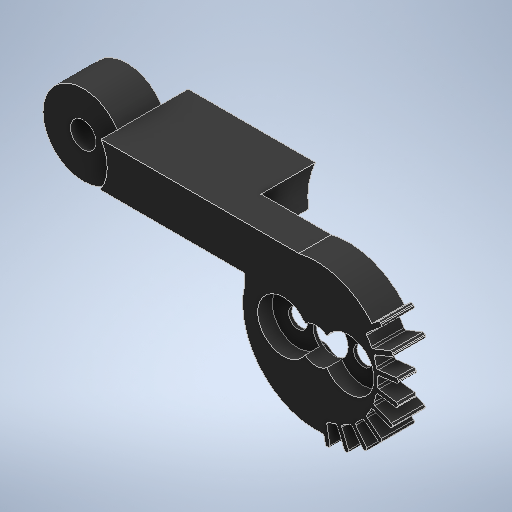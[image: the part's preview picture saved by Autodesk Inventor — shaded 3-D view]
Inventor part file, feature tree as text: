
AUTODESK INVENTOR PART (.ipt)
format: ipt  version: 2025.2 (Build 292293000, 293)  size: 515,072 bytes
history: native  units: mm
features: sketch x9, extrude x8, fillet x4, other x1, hole x1
ambient origin geometry x8: Origin, YZ Plane, XZ Plane, XY Plane, X Axis, Y Axis, Z Axis, Center Point
bodies: Body1 (feature_tree)
feature tree (23):
  other  "Sólido1"
  sketch  "Esboço1"  dims[d0=11.0mm d1=20.0mm]
  extrude  "Extrusão1"  Depth=11.0mm
  extrude  "Extrusão2"  Depth=6.8mm
  extrude  "Extrusão3"  Depth=21.0mm
  extrude  "Extrusão4"  Depth=6.0mm TaperAngle=0.0deg
  hole  "Furo2"  [1 undecoded]
  fillet  "Arredondamento1"  Radius=16.8mm
  fillet  "Arredondamento2"  Radius=8.726646mm
  fillet  "Arredondamento3"  Radius=1.3mm
  fillet  "Arredondamento4"  Radius=0.65mm
  extrude  "Extrusão5"  TaperAngle=90.0deg  [1 undecoded]
  extrude  "Extrusão6"  TaperAngle=90.0deg  [1 undecoded]
  extrude  "Extrusão7"  Depth=70.0mm TaperAngle=90.0deg
  extrude  "Extrusão8"  TaperAngle=90.0deg  [1 undecoded]
  sketch  "Esboço2"  dims[d2=34.0mm d3=6.8mm]
  sketch  "Esboço - Padrão circular2"  dims[d4=27.0mm d8=21.0mm]
  sketch  "Esboço - Padrão circular3"  dims[d9=4.45mm d10=0.0mm d11=6.0mm d12=0.0mm]
  sketch  "Esboço4"  dims[d13=4.45mm d14=0.0mm d15=7.45mm d16=0.0mm d17=16.8mm d18=8.726646mm d24=1.3mm d25=0.65mm]
  sketch  "Esboço5"  dims[d26=90.0deg d29=90.0deg]
  sketch  "Esboço6"  dims[d35=2.740167mm d36=90.0deg]
  sketch  "Esboço7"  dims[d37=90.0deg d38=70.0mm d40=90.0deg]
  sketch  "Esboço8"  dims[d42=20.0mm d44=120.0deg d46=90.0deg d47=180.0deg d55=5.5mm d56=20.0mm d57=3.5mm d58=6.0mm d59=7.0mm d60=2.0mm d61=90.0deg d62=8.0mm d63=20.594885mm d64=0.25mm d65=0.25mm d66=0.25mm d67=0.25mm d69=4.3mm d70=3.5mm d71=1.3mm d72=0.0mm d81=4.8mm d82=7.0mm d83=4.45mm d84=4.45mm d85=2.0mm d86=0.0mm d87=4.8mm d88=2.6mm d89=4.45mm d90=4.45mm d91=0.0mm d92=0.0mm d93=9.29mm d94=2.0mm d95=0.0mm d96=7.0mm d97=2.0mm d98=5.0mm d99=11.0mm d19=0.5mm d20=0.872665mm]
note: 4 required parameter values undecoded (feature->parameter linkage not recoverable at this tier; creation-order binding heuristic only, values carry confidence <= 0.55)
